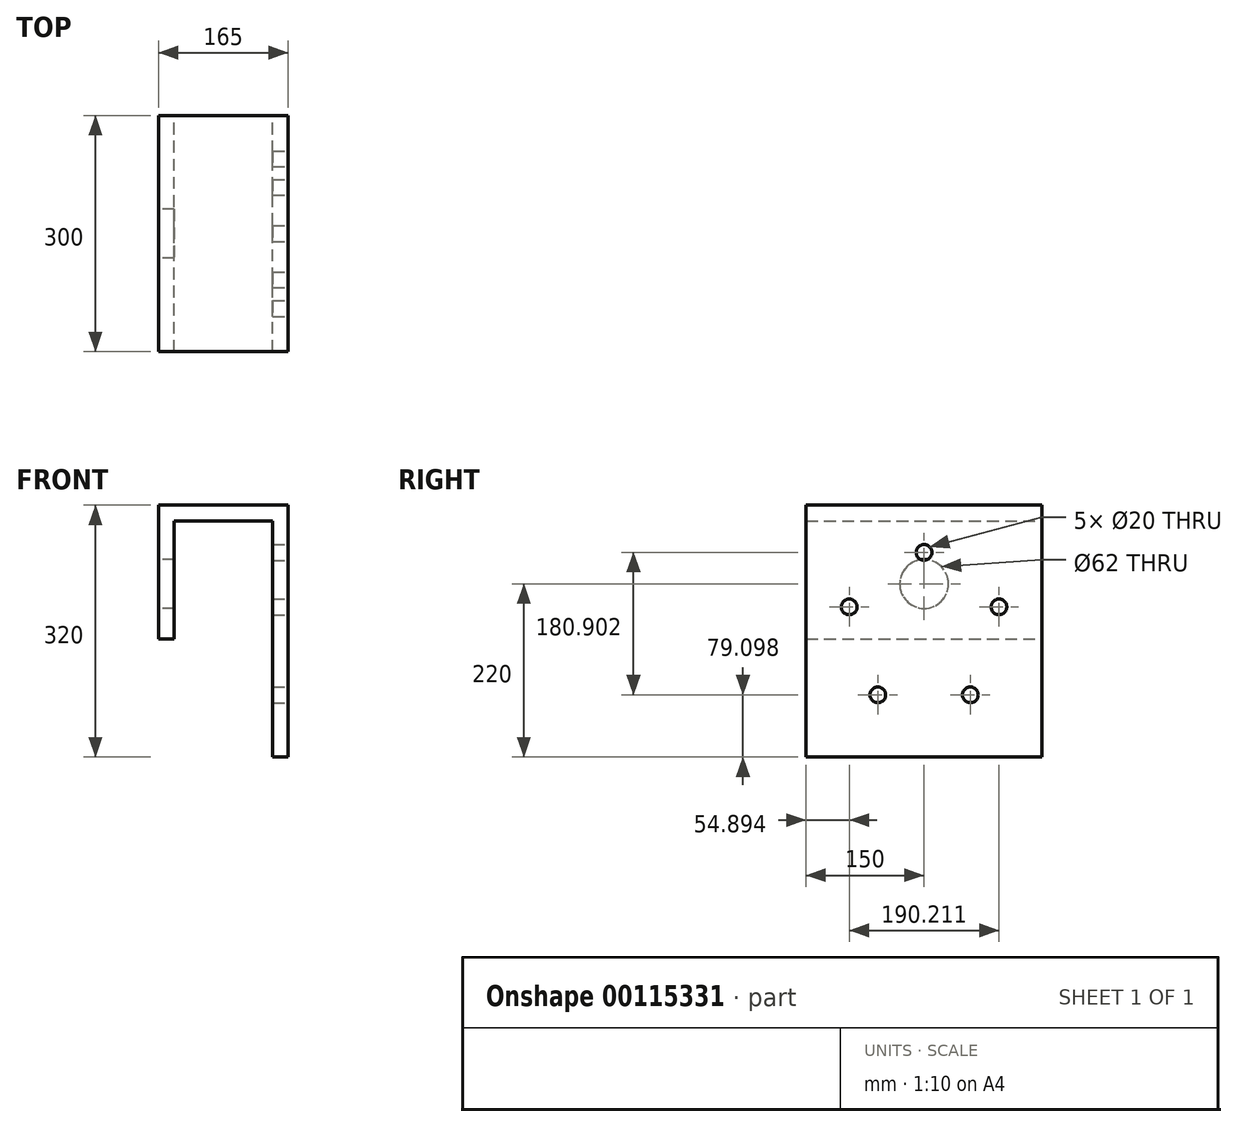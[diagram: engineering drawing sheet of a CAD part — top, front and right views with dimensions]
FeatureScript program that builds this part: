
annotation { "Feature Type Name" : "Feature", "Feature Type Description" : "" }
export const myFeature = defineFeature(function(context is Context, id is Id, definition is map)
    precondition{}
    {
        {
            var Q0;
            Q0=qCreatedBy(makeId("Front.planeOp"),FACE);
            var sketch = newSketch(context, id + "F0", { "sketchPlane" : qUnion([Q0])});
            skLineSegment(sketch, "E0", {"start": v(0, 0) * mm, "end": v(0, -170) * mm});
            skLineSegment(sketch, "E1", {"start": v(0, -170) * mm, "end": v(20, -170) * mm});
            skLineSegment(sketch, "E2.0", {"start": v(20, -20) * mm, "end": v(145, -20) * mm});
            skLineSegment(sketch, "E3", {"start": v(20, -170) * mm, "end": v(20, -20) * mm});
            skLineSegment(sketch, "E4", {"start": v(0, 0) * mm, "end": v(165, 0) * mm});
            skLineSegment(sketch, "E5", {"start": v(165, 0) * mm, "end": v(165, -20) * mm});
            skLineSegment(sketch, "E6", {"start": v(165, -20) * mm, "end": v(165, -320) * mm});
            skLineSegment(sketch, "E7.0", {"start": v(145, -20) * mm, "end": v(145, -320) * mm});
            skLineSegment(sketch, "E8", {"start": v(145, -320) * mm, "end": v(165, -320) * mm});
            skSolve(sketch);
        }
        {
            var Q0;
            Q0=makeQuery(id+"F0.imprint","IMPRINT",FACE,{"disambiguationData":[TD([[makeQuery(id+"F0.imprint","IMPRINT",EDGE,{"derivedFrom":sQuery(id+"F0.wireOp",EDGE,"E0")}),1.0]])]});
            extrude(context, id + "F1", {"entities" : qUnion([Q0]), "depth" : 300 * mm});
        }
        {
            var Q0;
            Q0=makeQuery(id+"F1.opExtrude","SWEPT_FACE",FACE,{"disambiguationData":[OSD([sQuery(id+"F0.wireOp",EDGE,"E0")])]});
            var sketch = newSketch(context, id + "F2", { "sketchPlane" : qUnion([Q0])});
            skCircle(sketch, "E9", {"center": v(150, -100) * mm, "radius": 31 * mm});
            skSolve(sketch);
        }
        {
            var Q0;
            Q0 = qSketchRegion(id + "F2", true);
            extrude(context, id + "F3", {"entities" : qUnion([Q0]), "operationType" : NewBodyOperationType.REMOVE, "endBound" : BoundingType.UP_TO_NEXT, "oppositeDirection" : true, "depth" : 25 * mm});
        }
        {
            var Q0;
            Q0=makeQuery(id+"F1.opExtrude","SWEPT_FACE",FACE,{"disambiguationData":[OSD([sQuery(id+"F0.wireOp",EDGE,"E5"),sQuery(id+"F0.wireOp",EDGE,"E6")])]});
            var sketch = newSketch(context, id + "F4", { "sketchPlane" : qUnion([Q0])});
            skPoint(sketch, "E10.endSnap0", {"position": v(-150, 0) * mm});
            skCircle(sketch, "E11", {"center": v(-150, -60) * mm, "radius": 10 * mm});
            skCircle(sketch, "E12.1.0", {"center": v(-245.1, -129.1) * mm, "radius": 10 * mm});
            skCircle(sketch, "E12.2.0", {"center": v(-208.78, -240.9) * mm, "radius": 10 * mm});
            skCircle(sketch, "E12.3.0", {"center": v(-91.22, -240.9) * mm, "radius": 10 * mm});
            skCircle(sketch, "E12.4.0", {"center": v(-54.9, -129.1) * mm, "radius": 10 * mm});
            skPoint(sketch, "E12.center", {"position": v(-150, -160) * mm});
            skSolve(sketch);
        }
        {
            var Q0;
            Q0 = qSketchRegion(id + "F4", true);
            extrude(context, id + "F5", {"entities" : qUnion([Q0]), "operationType" : NewBodyOperationType.REMOVE, "endBound" : BoundingType.UP_TO_NEXT, "oppositeDirection" : true, "depth" : 25 * mm});
        }
    });
